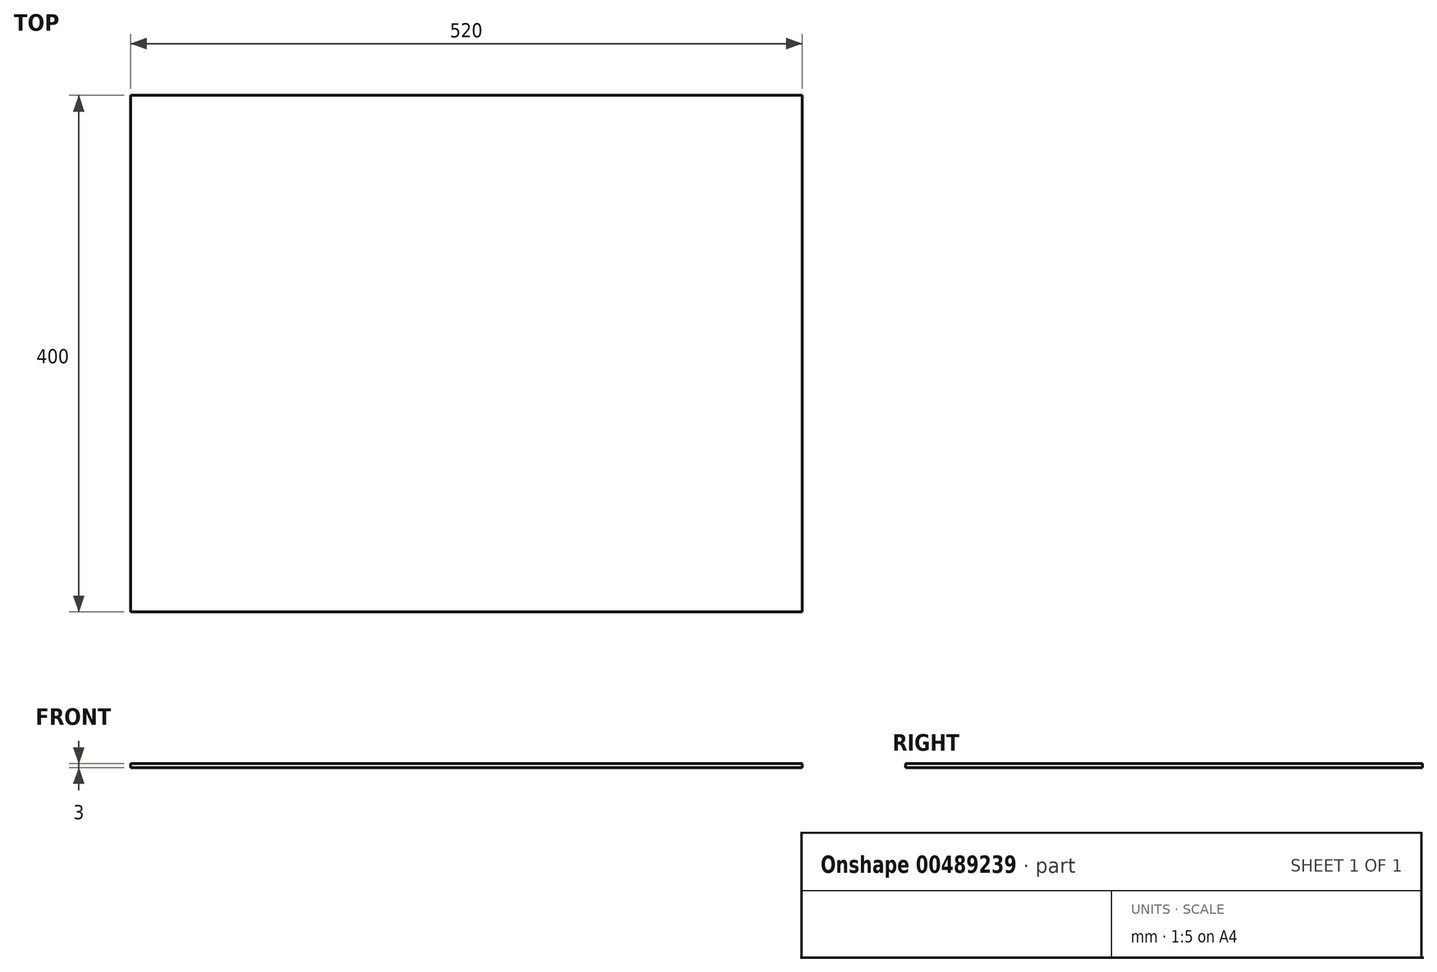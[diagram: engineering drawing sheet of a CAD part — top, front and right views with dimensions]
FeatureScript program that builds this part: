
annotation { "Feature Type Name" : "Feature", "Feature Type Description" : "" }
export const myFeature = defineFeature(function(context is Context, id is Id, definition is map)
    precondition{}
    {
        {
            var Q0;
            Q0=qCreatedBy(makeId("Top.planeOp"),FACE);
            var sketch = newSketch(context, id + "F0", { "sketchPlane" : qUnion([Q0])});
            skLineSegment(sketch, "E0.bottom", {"start": v(-251.67, 254.44) * mm, "end": v(268.33, 254.44) * mm});
            skLineSegment(sketch, "E0.top", {"start": v(-251.67, -145.56) * mm, "end": v(268.33, -145.56) * mm});
            skLineSegment(sketch, "E0.left", {"start": v(-251.67, 254.44) * mm, "end": v(-251.67, -145.56) * mm});
            skLineSegment(sketch, "E0.right", {"start": v(268.33, 254.44) * mm, "end": v(268.33, -145.56) * mm});
            skSolve(sketch);
        }
        {
            var Q0;
            Q0 = qSketchRegion(id + "F0", true);
            extrude(context, id + "F1", {"entities" : qUnion([Q0]), "depth" : 3 * mm});
        }
    });
